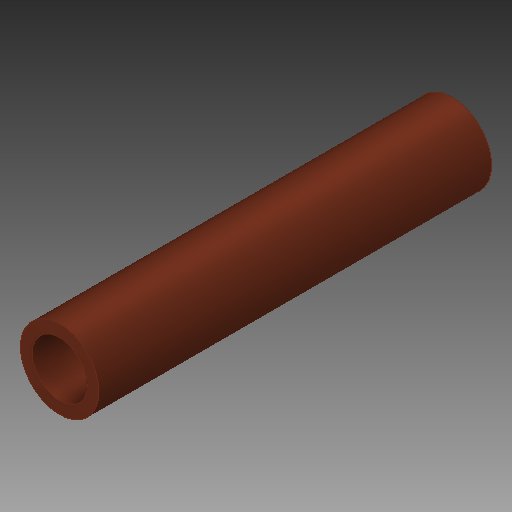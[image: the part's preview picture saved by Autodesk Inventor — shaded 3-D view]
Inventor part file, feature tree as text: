
AUTODESK INVENTOR PART (.ipt)
format: ipt  version: 2019 (Build 230136000, 136)  size: 93,696 bytes
history: native  units: in
note: dims shown in document units (in); Inventor stores cm internally (conversion verified against a paired STEP export)
features: other x3, sketch x2
ambient origin geometry x8: Origin, YZ Plane, XZ Plane, XY Plane, X Axis, Y Axis, Z Axis, Center Point
bodies: Solid1 (feature_tree)
feature tree (5):
  other  "project roller 2 part1.ipt"
  other  "Solid1::project roller 2 part1.ipt"
  other  "TaggingFeature1"
  sketch  "Sketch1"  dims[d0=0.3937in]
  sketch  "Sketch2"
